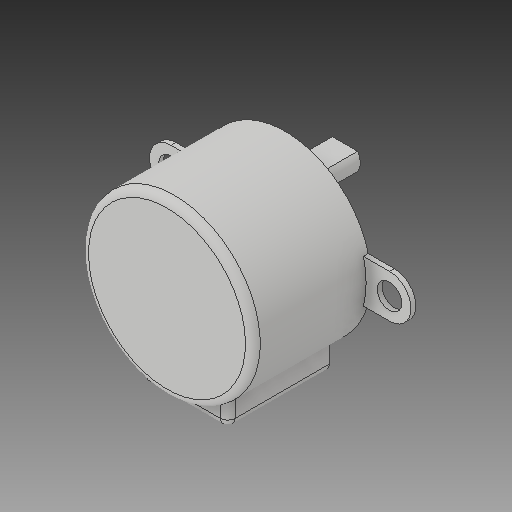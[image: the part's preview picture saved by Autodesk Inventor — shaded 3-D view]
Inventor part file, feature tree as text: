
AUTODESK INVENTOR PART (.ipt)
format: ipt  version: 2017 (Build 210142000, 142)  size: 200,704 bytes
history: native  units: mm
features: extrude x7, sketch x2, fillet x1
ambient origin geometry x8: Origin, YZ Plane, XZ Plane, XY Plane, X Axis, Y Axis, Z Axis, Center Point
bodies: Solid1 (feature_tree)
feature tree (10):
  sketch  "Sketch1"  dims[d0=13.95mm d1=7.18mm]
  extrude  "Extrusion1"  Depth=13.95mm
  extrude  "Extrusion2"  Depth=2.0mm
  extrude  "Extrusion3"  Depth=2.0mm
  extrude  "Extrusion4"  Depth=19.2mm TaperAngle=0.0deg
  extrude  "Extrusion5"  Depth=2.0mm TaperAngle=0.0deg
  extrude  "Extrusion6"  Depth=2.0mm TaperAngle=0.0deg
  fillet  "Fillet1"  Radius=9.22mm
  extrude  "Extrusion7"  Depth=2.0mm
  sketch  "Sketch2"  dims[d2=4.46mm d3=3.5mm d4=4.0mm d5=19.2mm d6=0.0mm d7=0.79mm d8=0.0mm d9=16.5mm d10=0.0mm d11=9.22mm d12=5.0mm d13=2.85mm d14=1.75mm d15=0.0mm d16=3.78mm d17=0.0mm d18=9.73mm d19=0.0mm d20=1.2mm d21=2.0mm d22=1.12mm d23=6.0mm d24=2.0mm d25=0.0mm d26=35.5mm]
